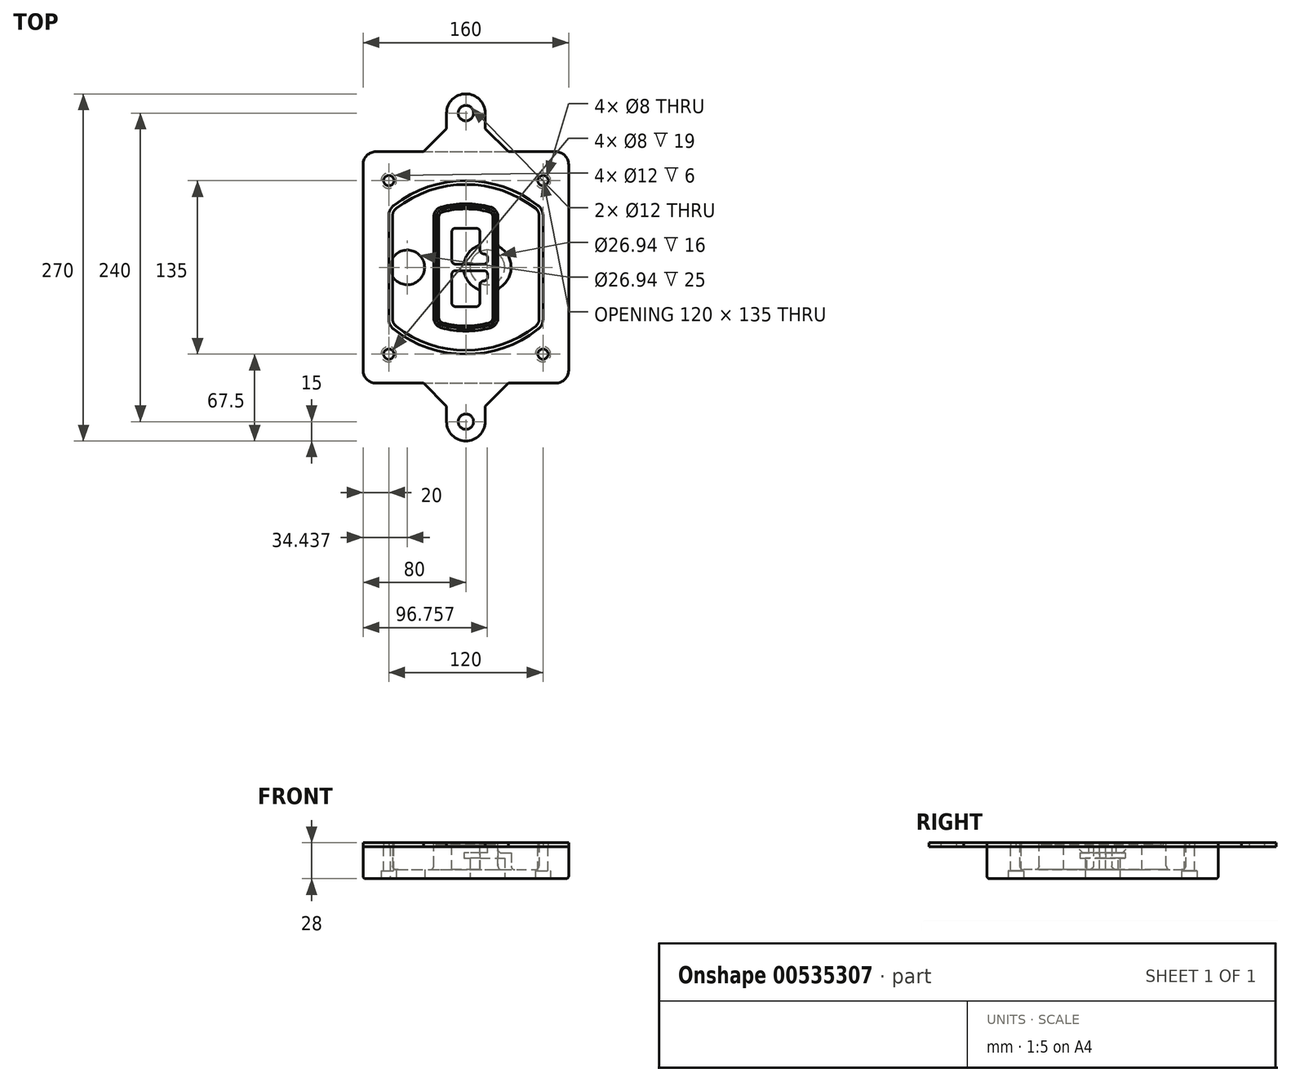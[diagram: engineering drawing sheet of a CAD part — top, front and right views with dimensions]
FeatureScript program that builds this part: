
annotation { "Feature Type Name" : "Feature", "Feature Type Description" : "" }
export const myFeature = defineFeature(function(context is Context, id is Id, definition is map)
    precondition{}
    {
        {
            var Q0;
            Q0=qCreatedBy(makeId("Top.planeOp"),FACE);
            var sketch = newSketch(context, id + "F0", { "sketchPlane" : qUnion([Q0])});
            skPoint(sketch, "E0.rect.middle", {"position": v(0, 0) * mm});
            skLineSegment(sketch, "E1.bottom", {"start": v(-70, -90) * mm, "end": v(70, -90) * mm});
            skLineSegment(sketch, "E1.top", {"start": v(-70, 90) * mm, "end": v(70, 90) * mm});
            skLineSegment(sketch, "E1.left", {"start": v(-80, -80) * mm, "end": v(-80, 80) * mm});
            skLineSegment(sketch, "E1.right", {"start": v(80, -80) * mm, "end": v(80, 80) * mm});
            skLineSegment(sketch, "E2", {"start": v(-80, 90) * mm, "end": v(80, -90) * mm, "construction": true});
            skLineSegment(sketch, "E3", {"start": v(80, 90) * mm, "end": v(-80, -90) * mm, "construction": true});
            skCircle(sketch, "E4", {"center": v(-60, 67.5) * mm, "radius": 4 * mm});
            skCircle(sketch, "E5", {"center": v(60, 67.5) * mm, "radius": 4 * mm});
            skCircle(sketch, "E6", {"center": v(60, -67.5) * mm, "radius": 4 * mm});
            skCircle(sketch, "E7", {"center": v(-60, -67.5) * mm, "radius": 4 * mm});
            skLineSegment(sketch, "E8", {"start": v(-60, 67.5) * mm, "end": v(60, 67.5) * mm, "construction": true});
            skLineSegment(sketch, "E9", {"start": v(60, 67.5) * mm, "end": v(60, -67.5) * mm, "construction": true});
            skLineSegment(sketch, "E10", {"start": v(60, -67.5) * mm, "end": v(-60, -67.5) * mm, "construction": true});
            skLineSegment(sketch, "E11", {"start": v(-60, -67.5) * mm, "end": v(-60, 67.5) * mm, "construction": true});
            skLineSegment(sketch, "E12", {"start": v(-60, 40.3) * mm, "end": v(-60, -40.3) * mm});
            skLineSegment(sketch, "E13", {"start": v(60, 40.3) * mm, "end": v(60, -40.3) * mm});
            skArc(sketch, "E14", {"start": v(56.15, 48.18) * mm, "mid": v(0, 67.5) * mm, "end": v(-56.15, 48.18) * mm});
            skArc(sketch, "E15", {"start": v(-56.15, -48.18) * mm, "mid": v(0, -67.5) * mm, "end": v(56.15, -48.18) * mm});
            skLineSegment(sketch, "E16", {"start": v(-60, 0) * mm, "end": v(60, 0) * mm, "construction": true});
            skPoint(sketch, "E17.visualSharp", {"position": v(-60, -45) * mm});
            skArc(sketch, "E17.filletArc", {"start": v(-60, -40.3) * mm, "mid": v(-58.99, -44.68) * mm, "end": v(-56.15, -48.18) * mm});
            skPoint(sketch, "E18.visualSharp", {"position": v(-60, 45) * mm});
            skArc(sketch, "E18.filletArc", {"start": v(-56.15, 48.18) * mm, "mid": v(-58.99, 44.68) * mm, "end": v(-60, 40.3) * mm});
            skPoint(sketch, "E19.visualSharp", {"position": v(60, 45) * mm});
            skArc(sketch, "E19.filletArc", {"start": v(60, 40.3) * mm, "mid": v(58.99, 44.68) * mm, "end": v(56.15, 48.18) * mm});
            skPoint(sketch, "E20.visualSharp", {"position": v(60, -45) * mm});
            skArc(sketch, "E20.filletArc", {"start": v(56.15, -48.18) * mm, "mid": v(58.99, -44.68) * mm, "end": v(60, -40.3) * mm});
            skPoint(sketch, "E21.visualSharp", {"position": v(-80, 90) * mm});
            skArc(sketch, "E21.filletArc", {"start": v(-70, 90) * mm, "mid": v(-77.07, 87.07) * mm, "end": v(-80, 80) * mm});
            skPoint(sketch, "E22.visualSharp", {"position": v(80, 90) * mm});
            skArc(sketch, "E22.filletArc", {"start": v(80, 80) * mm, "mid": v(77.07, 87.07) * mm, "end": v(70, 90) * mm});
            skPoint(sketch, "E23.visualSharp", {"position": v(80, -90) * mm});
            skArc(sketch, "E23.filletArc", {"start": v(70, -90) * mm, "mid": v(77.07, -87.07) * mm, "end": v(80, -80) * mm});
            skPoint(sketch, "E24.visualSharp", {"position": v(-80, -90) * mm});
            skArc(sketch, "E24.filletArc", {"start": v(-80, -80) * mm, "mid": v(-77.07, -87.07) * mm, "end": v(-70, -90) * mm});
            skArc(sketch, "E25.0", {"start": v(57, 40.3) * mm, "mid": v(56.3, 43.36) * mm, "end": v(54.3, 45.81) * mm});
            skLineSegment(sketch, "E25.1", {"start": v(57, 40.3) * mm, "end": v(57, -40.3) * mm});
            skArc(sketch, "E25.2", {"start": v(54.3, -45.81) * mm, "mid": v(56.3, -43.36) * mm, "end": v(57, -40.3) * mm});
            skArc(sketch, "E25.3", {"start": v(-54.3, -45.81) * mm, "mid": v(0, -64.5) * mm, "end": v(54.3, -45.81) * mm});
            skArc(sketch, "E25.4", {"start": v(-57, -40.3) * mm, "mid": v(-56.3, -43.36) * mm, "end": v(-54.3, -45.81) * mm});
            skArc(sketch, "E25.5", {"start": v(54.3, 45.81) * mm, "mid": v(0, 64.5) * mm, "end": v(-54.3, 45.81) * mm});
            skLineSegment(sketch, "E25.6", {"start": v(-57, 40.3) * mm, "end": v(-57, -40.3) * mm});
            skArc(sketch, "E25.7", {"start": v(-54.3, 45.81) * mm, "mid": v(-56.3, 43.36) * mm, "end": v(-57, 40.3) * mm});
            skArc(sketch, "E26.0", {"start": v(-58.62, 51.33) * mm, "mid": v(-62.58, 46.43) * mm, "end": v(-64, 40.3) * mm});
            skArc(sketch, "E26.1", {"start": v(58.62, 51.33) * mm, "mid": v(0, 71.5) * mm, "end": v(-58.62, 51.33) * mm});
            skArc(sketch, "E26.2", {"start": v(64, 40.3) * mm, "mid": v(62.58, 46.43) * mm, "end": v(58.62, 51.33) * mm});
            skLineSegment(sketch, "E26.3", {"start": v(64, 40.3) * mm, "end": v(64, -40.3) * mm});
            skArc(sketch, "E26.4", {"start": v(58.62, -51.33) * mm, "mid": v(62.58, -46.43) * mm, "end": v(64, -40.3) * mm});
            skLineSegment(sketch, "E26.5", {"start": v(-64, 40.3) * mm, "end": v(-64, -40.3) * mm});
            skArc(sketch, "E26.6", {"start": v(-58.62, -51.33) * mm, "mid": v(0, -71.5) * mm, "end": v(58.62, -51.33) * mm});
            skArc(sketch, "E26.7", {"start": v(-64, -40.3) * mm, "mid": v(-62.58, -46.43) * mm, "end": v(-58.62, -51.33) * mm});
            skSolve(sketch);
        }
        {
            var Q0;
            Q0=makeQuery(id+"F0.imprint","IMPRINT",FACE,{"disambiguationData":[TD([[makeQuery(id+"F0.imprint","IMPRINT",EDGE,{"derivedFrom":sQuery(id+"F0.wireOp",EDGE,"E1.bottom")}),1.0]])]});
            var Q1;
            Q1=makeQuery(id+"F0.imprint","IMPRINT",FACE,{"disambiguationData":[TD([[makeQuery(id+"F0.imprint","IMPRINT",EDGE,{"derivedFrom":sQuery(id+"F0.wireOp",EDGE,"E12")}),1.0]])]});
            var Q2;
            Q2=makeQuery(id+"F0.imprint","IMPRINT",FACE,{"disambiguationData":[TD([[makeQuery(id+"F0.imprint","IMPRINT",EDGE,{"derivedFrom":sQuery(id+"F0.wireOp",EDGE,"E25.0")}),1.0]])]});
            var Q3;
            Q3=makeQuery(id+"F0.imprint","IMPRINT",FACE,{"disambiguationData":[TD([[makeQuery(id+"F0.imprint","IMPRINT",EDGE,{"derivedFrom":sQuery(id+"F0.wireOp",EDGE,"E12")}),-1.0]])]});
            extrude(context, id + "F1", {"entities" : qUnion([Q0, Q1, Q2, Q3]), "oppositeDirection" : true, "depth" : 25 * mm});
        }
        {
            var Q0;
            Q0=makeQuery(id+"F0.imprint","IMPRINT",FACE,{"disambiguationData":[TD([[makeQuery(id+"F0.imprint","IMPRINT",EDGE,{"derivedFrom":sQuery(id+"F0.wireOp",EDGE,"E12")}),1.0]])]});
            extrude(context, id + "F2", {"entities" : qUnion([Q0]), "operationType" : NewBodyOperationType.ADD, "depth" : 3 * mm});
        }
        {
            var Q0;
            Q0=makeQuery(id+"F0.imprint","IMPRINT",FACE,{"disambiguationData":[TD([[makeQuery(id+"F0.imprint","IMPRINT",EDGE,{"derivedFrom":sQuery(id+"F0.wireOp",EDGE,"E25.0")}),1.0]])]});
            extrude(context, id + "F3", {"entities" : qUnion([Q0]), "operationType" : NewBodyOperationType.REMOVE, "oppositeDirection" : true, "depth" : 18 * mm});
        }
        {
            var Q0;
            Q0=makeQuery(id+"F2.opExtrude","CAP_FACE",FACE,{"disambiguationData":[OSD([sQuery(id+"F0.wireOp",EDGE,"E12"),sQuery(id+"F0.wireOp",EDGE,"E13"),sQuery(id+"F0.wireOp",EDGE,"E14"),sQuery(id+"F0.wireOp",EDGE,"E15"),sQuery(id+"F0.wireOp",EDGE,"E17.filletArc"),sQuery(id+"F0.wireOp",EDGE,"E18.filletArc"),sQuery(id+"F0.wireOp",EDGE,"E19.filletArc"),sQuery(id+"F0.wireOp",EDGE,"E20.filletArc"),sQuery(id+"F0.wireOp",EDGE,"E25.0"),sQuery(id+"F0.wireOp",EDGE,"E25.1"),sQuery(id+"F0.wireOp",EDGE,"E25.2"),sQuery(id+"F0.wireOp",EDGE,"E25.3"),sQuery(id+"F0.wireOp",EDGE,"E25.4"),sQuery(id+"F0.wireOp",EDGE,"E25.5"),sQuery(id+"F0.wireOp",EDGE,"E25.6"),sQuery(id+"F0.wireOp",EDGE,"E25.7")])],"isStart":false});
            var sketch = newSketch(context, id + "F4", { "sketchPlane" : qUnion([Q0])});
            skArc(sketch, "E27.0", {"start": v(-19.08, -46.97) * mm, "mid": v(0, -49.5) * mm, "end": v(19.08, -46.97) * mm});
            skArc(sketch, "E28.0", {"start": v(19.08, 46.97) * mm, "mid": v(0, 49.5) * mm, "end": v(-19.08, 46.97) * mm});
            skLineSegment(sketch, "E29", {"start": v(-25, 39.25) * mm, "end": v(-25, -39.25) * mm});
            skLineSegment(sketch, "E30", {"start": v(25, 39.25) * mm, "end": v(25, -39.25) * mm});
            skLineSegment(sketch, "E31", {"start": v(-25, 45.1) * mm, "end": v(25, 45.1) * mm, "construction": true});
            skLineSegment(sketch, "E32", {"start": v(-25, -45.1) * mm, "end": v(25, -45.1) * mm, "construction": true});
            skPoint(sketch, "E33.visualSharp", {"position": v(-25, 45.1) * mm});
            skArc(sketch, "E33.filletArc", {"start": v(-19.08, 46.97) * mm, "mid": v(-23.35, 44.11) * mm, "end": v(-25, 39.25) * mm});
            skPoint(sketch, "E34.visualSharp", {"position": v(25, 45.1) * mm});
            skArc(sketch, "E34.filletArc", {"start": v(25, 39.25) * mm, "mid": v(23.35, 44.11) * mm, "end": v(19.08, 46.97) * mm});
            skPoint(sketch, "E35.visualSharp", {"position": v(25, -45.1) * mm});
            skArc(sketch, "E35.filletArc", {"start": v(19.08, -46.97) * mm, "mid": v(23.35, -44.11) * mm, "end": v(25, -39.25) * mm});
            skPoint(sketch, "E36.visualSharp", {"position": v(-25, -45.1) * mm});
            skArc(sketch, "E36.filletArc", {"start": v(-25, -39.25) * mm, "mid": v(-23.35, -44.11) * mm, "end": v(-19.08, -46.97) * mm});
            skArc(sketch, "E37.0", {"start": v(54.3, 45.81) * mm, "mid": v(0, 64.5) * mm, "end": v(-54.3, 45.81) * mm});
            skArc(sketch, "E37.1", {"start": v(-54.3, 45.81) * mm, "mid": v(-56.3, 43.36) * mm, "end": v(-57, 40.3) * mm});
            skLineSegment(sketch, "E37.2", {"start": v(-57, 40.3) * mm, "end": v(-57, -40.3) * mm});
            skArc(sketch, "E37.3", {"start": v(-57, -40.3) * mm, "mid": v(-56.3, -43.36) * mm, "end": v(-54.3, -45.81) * mm});
            skArc(sketch, "E37.4", {"start": v(-54.3, -45.81) * mm, "mid": v(0, -64.5) * mm, "end": v(54.3, -45.81) * mm});
            skArc(sketch, "E37.5", {"start": v(54.3, -45.81) * mm, "mid": v(56.3, -43.36) * mm, "end": v(57, -40.3) * mm});
            skLineSegment(sketch, "E37.6", {"start": v(57, 40.3) * mm, "end": v(57, -40.3) * mm});
            skArc(sketch, "E37.7", {"start": v(57, 40.3) * mm, "mid": v(56.3, 43.36) * mm, "end": v(54.3, 45.81) * mm});
            skLineSegment(sketch, "E38.0", {"start": v(23, 39.25) * mm, "end": v(23, -39.25) * mm});
            skArc(sketch, "E38.1", {"start": v(18.56, -45.04) * mm, "mid": v(21.76, -42.9) * mm, "end": v(23, -39.25) * mm});
            skArc(sketch, "E38.2", {"start": v(-18.56, -45.04) * mm, "mid": v(0, -47.5) * mm, "end": v(18.56, -45.04) * mm});
            skArc(sketch, "E38.3", {"start": v(-23, -39.25) * mm, "mid": v(-21.76, -42.9) * mm, "end": v(-18.56, -45.04) * mm});
            skLineSegment(sketch, "E38.4", {"start": v(-23, 39.25) * mm, "end": v(-23, -39.25) * mm});
            skArc(sketch, "E38.5", {"start": v(23, 39.25) * mm, "mid": v(21.76, 42.9) * mm, "end": v(18.56, 45.04) * mm});
            skArc(sketch, "E38.6", {"start": v(-18.56, 45.04) * mm, "mid": v(-21.76, 42.9) * mm, "end": v(-23, 39.25) * mm});
            skArc(sketch, "E38.7", {"start": v(18.56, 45.04) * mm, "mid": v(0, 47.5) * mm, "end": v(-18.56, 45.04) * mm});
            skArc(sketch, "E39.0", {"start": v(21, 39.25) * mm, "mid": v(20.18, 41.68) * mm, "end": v(18.04, 43.1) * mm});
            skLineSegment(sketch, "E39.1", {"start": v(21, 39.25) * mm, "end": v(21, -39.25) * mm});
            skArc(sketch, "E39.2", {"start": v(18.04, -43.1) * mm, "mid": v(20.18, -41.68) * mm, "end": v(21, -39.25) * mm});
            skArc(sketch, "E39.3", {"start": v(-18.04, -43.1) * mm, "mid": v(0, -45.5) * mm, "end": v(18.04, -43.1) * mm});
            skArc(sketch, "E39.4", {"start": v(-21, -39.25) * mm, "mid": v(-20.18, -41.68) * mm, "end": v(-18.04, -43.1) * mm});
            skArc(sketch, "E39.5", {"start": v(18.04, 43.1) * mm, "mid": v(0, 45.5) * mm, "end": v(-18.04, 43.1) * mm});
            skLineSegment(sketch, "E39.6", {"start": v(-21, 39.25) * mm, "end": v(-21, -39.25) * mm});
            skArc(sketch, "E39.7", {"start": v(-18.04, 43.1) * mm, "mid": v(-20.18, 41.68) * mm, "end": v(-21, 39.25) * mm});
            skLineSegment(sketch, "E40", {"start": v(-25, 0) * mm, "end": v(25, 0) * mm, "construction": true});
            skLineSegment(sketch, "E41", {"start": v(-11, 5.5) * mm, "end": v(-11, 27.5) * mm});
            skLineSegment(sketch, "E42", {"start": v(-8, 30.5) * mm, "end": v(8, 30.5) * mm});
            skLineSegment(sketch, "E43", {"start": v(11, 27.5) * mm, "end": v(11, 13.5) * mm});
            skLineSegment(sketch, "E44", {"start": v(14, 10.5) * mm, "end": v(14, 10.5) * mm});
            skLineSegment(sketch, "E45", {"start": v(17, 7.5) * mm, "end": v(17, 5.5) * mm});
            skLineSegment(sketch, "E46", {"start": v(14, 2.5) * mm, "end": v(-8, 2.5) * mm});
            skPoint(sketch, "E47.visualSharp", {"position": v(-11, 30.5) * mm});
            skArc(sketch, "E47.filletArc", {"start": v(-8, 30.5) * mm, "mid": v(-10.12, 29.62) * mm, "end": v(-11, 27.5) * mm});
            skPoint(sketch, "E48.visualSharp", {"position": v(11, 30.5) * mm});
            skArc(sketch, "E48.filletArc", {"start": v(11, 27.5) * mm, "mid": v(10.12, 29.62) * mm, "end": v(8, 30.5) * mm});
            skPoint(sketch, "E49.visualSharp", {"position": v(11, 10.5) * mm});
            skArc(sketch, "E49.filletArc", {"start": v(11, 13.5) * mm, "mid": v(11.88, 11.38) * mm, "end": v(14, 10.5) * mm});
            skPoint(sketch, "E50.visualSharp", {"position": v(17, 10.5) * mm});
            skArc(sketch, "E50.filletArc", {"start": v(17, 7.5) * mm, "mid": v(16.12, 9.62) * mm, "end": v(14, 10.5) * mm});
            skPoint(sketch, "E51.visualSharp", {"position": v(17, 2.5) * mm});
            skArc(sketch, "E51.filletArc", {"start": v(14, 2.5) * mm, "mid": v(16.12, 3.38) * mm, "end": v(17, 5.5) * mm});
            skPoint(sketch, "E52.visualSharp", {"position": v(-11, 2.5) * mm});
            skArc(sketch, "E52.filletArc", {"start": v(-11, 5.5) * mm, "mid": v(-10.12, 3.38) * mm, "end": v(-8, 2.5) * mm});
            skLineSegment(sketch, "E53.0.MirrorCS", {"start": v(14, -2.5) * mm, "end": v(-8, -2.5) * mm});
            skArc(sketch, "E54.0.MirrorCS", {"start": v(-11, -5.5) * mm, "mid": v(-10.12, -3.38) * mm, "end": v(-8, -2.5) * mm});
            skLineSegment(sketch, "E55.0.MirrorCS", {"start": v(-11, -5.5) * mm, "end": v(-11, -27.5) * mm});
            skArc(sketch, "E56.0.MirrorCS", {"start": v(-8, -30.5) * mm, "mid": v(-10.12, -29.62) * mm, "end": v(-11, -27.5) * mm});
            skLineSegment(sketch, "E57.0.MirrorCS", {"start": v(-8, -30.5) * mm, "end": v(8, -30.5) * mm});
            skArc(sketch, "E58.0.MirrorCS", {"start": v(11, -27.5) * mm, "mid": v(10.12, -29.62) * mm, "end": v(8, -30.5) * mm});
            skLineSegment(sketch, "E59.0.MirrorCS", {"start": v(11, -27.5) * mm, "end": v(11, -13.5) * mm});
            skArc(sketch, "E60.0.MirrorCS", {"start": v(11, -13.5) * mm, "mid": v(11.88, -11.38) * mm, "end": v(14, -10.5) * mm});
            skArc(sketch, "E61.0.MirrorCS", {"start": v(17, -7.5) * mm, "mid": v(16.12, -9.62) * mm, "end": v(14, -10.5) * mm});
            skLineSegment(sketch, "E62.0.MirrorCS", {"start": v(17, -7.5) * mm, "end": v(17, -5.5) * mm});
            skArc(sketch, "E63.0.MirrorCS", {"start": v(14, -2.5) * mm, "mid": v(16.12, -3.38) * mm, "end": v(17, -5.5) * mm});
            skSolve(sketch);
        }
        {
            var Q0;
            Q0=makeQuery(id+"F4.imprint","IMPRINT",FACE,{"disambiguationData":[TD([[makeQuery(id+"F4.imprint","IMPRINT",EDGE,{"derivedFrom":sQuery(id+"F4.wireOp",EDGE,"E27.0")}),1.0]])]});
            var Q1;
            Q1=makeQuery(id+"F4.imprint","IMPRINT",FACE,{"disambiguationData":[TD([[makeQuery(id+"F4.imprint","IMPRINT",EDGE,{"derivedFrom":sQuery(id+"F4.wireOp",EDGE,"E38.0")}),-1.0]])]});
            var Q2;
            Q2=makeQuery(id+"F4.imprint","IMPRINT",FACE,{"disambiguationData":[TD([[makeQuery(id+"F4.imprint","IMPRINT",EDGE,{"derivedFrom":sQuery(id+"F4.wireOp",EDGE,"E39.0")}),1.0]])]});
            extrude(context, id + "F5", {"entities" : qUnion([Q0, Q1, Q2]), "operationType" : NewBodyOperationType.ADD, "endBound" : BoundingType.UP_TO_NEXT, "oppositeDirection" : true, "depth" : 25 * mm});
        }
        {
            var Q0;
            Q0=makeQuery(id+"F4.imprint","IMPRINT",FACE,{"disambiguationData":[TD([[makeQuery(id+"F4.imprint","IMPRINT",EDGE,{"derivedFrom":sQuery(id+"F4.wireOp",EDGE,"E38.0")}),-1.0]])]});
            extrude(context, id + "F6", {"entities" : qUnion([Q0]), "operationType" : NewBodyOperationType.REMOVE, "oppositeDirection" : true, "depth" : 2 * mm});
        }
        {
            var Q0;
            Q0=makeQuery(id+"F1.opExtrude","CAP_FACE",FACE,{"disambiguationData":[OSD([sQuery(id+"F0.wireOp",EDGE,"E1.bottom"),sQuery(id+"F0.wireOp",EDGE,"E1.top"),sQuery(id+"F0.wireOp",EDGE,"E1.left"),sQuery(id+"F0.wireOp",EDGE,"E1.right"),sQuery(id+"F0.wireOp",EDGE,"E4"),sQuery(id+"F0.wireOp",EDGE,"E5"),sQuery(id+"F0.wireOp",EDGE,"E6"),sQuery(id+"F0.wireOp",EDGE,"E7"),sQuery(id+"F0.wireOp",EDGE,"E21.filletArc"),sQuery(id+"F0.wireOp",EDGE,"E22.filletArc"),sQuery(id+"F0.wireOp",EDGE,"E23.filletArc"),sQuery(id+"F0.wireOp",EDGE,"E24.filletArc")])],"isStart":false});
            var sketch = newSketch(context, id + "F7", { "sketchPlane" : qUnion([Q0])});
            skCircle(sketch, "E64", {"center": v(16.76, 0) * mm, "radius": 13.47 * mm});
            skCircle(sketch, "E65", {"center": v(-45.56, 0) * mm, "radius": 13.47 * mm});
            skLineSegment(sketch, "E66", {"start": v(80, 0) * mm, "end": v(-80, 0) * mm});
            skCircle(sketch, "E67", {"center": v(16.76, 0) * mm, "radius": 18.47 * mm});
            skCircle(sketch, "E68", {"center": v(60, -67.5) * mm, "radius": 6 * mm});
            skCircle(sketch, "E69", {"center": v(-60, -67.5) * mm, "radius": 6 * mm});
            skCircle(sketch, "E70", {"center": v(-60, 67.5) * mm, "radius": 6 * mm});
            skCircle(sketch, "E71", {"center": v(60, 67.5) * mm, "radius": 6 * mm});
            skSolve(sketch);
        }
        {
            var Q0;
            {var subQ1=sQuery(id+"F7.wireOp",EDGE,"E66");var subQ4=sQuery(id+"F7.wireOp",EDGE,"E64");var subQ6=makeQuery(id+"F7.imprint","INTERSECT",VERTEX,{"disambiguationData":[OD(0.0)],"derivedFrom":[subQ4,subQ1]});Q0=makeQuery(id+"F7.imprint","IMPRINT",FACE,{"disambiguationData":[TD([[makeQuery(id+"F7.imprint","IMPRINT",EDGE,{"disambiguationData":[TD([[subQ6,-1.0]])],"derivedFrom":subQ4}),-1.0]])]});}
            var Q1;
            {var subQ0=sQuery(id+"F7.wireOp",EDGE,"E66");var subQ1=sQuery(id+"F7.wireOp",EDGE,"E64");var subQ3=makeQuery(id+"F7.imprint","INTERSECT",VERTEX,{"disambiguationData":[OD(0.0)],"derivedFrom":[subQ1,subQ0]});Q1=makeQuery(id+"F7.imprint","IMPRINT",FACE,{"disambiguationData":[TD([[makeQuery(id+"F7.imprint","IMPRINT",EDGE,{"disambiguationData":[TD([[subQ3,-1.0]])],"derivedFrom":subQ1}),1.0]])]});}
            var Q2;
            {var subQ0=sQuery(id+"F7.wireOp",EDGE,"E66");var subQ1=sQuery(id+"F7.wireOp",EDGE,"E64");var subQ3=makeQuery(id+"F7.imprint","INTERSECT",VERTEX,{"disambiguationData":[OD(0.0)],"derivedFrom":[subQ1,subQ0]});Q2=makeQuery(id+"F7.imprint","IMPRINT",FACE,{"disambiguationData":[TD([[makeQuery(id+"F7.imprint","IMPRINT",EDGE,{"disambiguationData":[TD([[subQ3,1.0]])],"derivedFrom":subQ1}),1.0]])]});}
            var Q3;
            {var subQ1=sQuery(id+"F7.wireOp",EDGE,"E66");var subQ4=sQuery(id+"F7.wireOp",EDGE,"E64");var subQ6=makeQuery(id+"F7.imprint","INTERSECT",VERTEX,{"disambiguationData":[OD(0.0)],"derivedFrom":[subQ4,subQ1]});Q3=makeQuery(id+"F7.imprint","IMPRINT",FACE,{"disambiguationData":[TD([[makeQuery(id+"F7.imprint","IMPRINT",EDGE,{"disambiguationData":[TD([[subQ6,1.0]])],"derivedFrom":subQ4}),-1.0]])]});}
            extrude(context, id + "F8", {"entities" : qUnion([Q0, Q1, Q2, Q3]), "operationType" : NewBodyOperationType.ADD, "oppositeDirection" : true, "depth" : 20 * mm});
        }
        {
            var Q0;
            {var subQ0=sQuery(id+"F7.wireOp",EDGE,"E66");var subQ1=sQuery(id+"F7.wireOp",EDGE,"E64");var subQ3=makeQuery(id+"F7.imprint","INTERSECT",VERTEX,{"disambiguationData":[OD(0.0)],"derivedFrom":[subQ1,subQ0]});Q0=makeQuery(id+"F7.imprint","IMPRINT",FACE,{"disambiguationData":[TD([[makeQuery(id+"F7.imprint","IMPRINT",EDGE,{"disambiguationData":[TD([[subQ3,-1.0]])],"derivedFrom":subQ1}),1.0]])]});}
            var Q1;
            {var subQ0=sQuery(id+"F7.wireOp",EDGE,"E66");var subQ1=sQuery(id+"F7.wireOp",EDGE,"E64");var subQ3=makeQuery(id+"F7.imprint","INTERSECT",VERTEX,{"disambiguationData":[OD(0.0)],"derivedFrom":[subQ1,subQ0]});Q1=makeQuery(id+"F7.imprint","IMPRINT",FACE,{"disambiguationData":[TD([[makeQuery(id+"F7.imprint","IMPRINT",EDGE,{"disambiguationData":[TD([[subQ3,1.0]])],"derivedFrom":subQ1}),1.0]])]});}
            extrude(context, id + "F9", {"entities" : qUnion([Q0, Q1]), "operationType" : NewBodyOperationType.REMOVE, "oppositeDirection" : true, "depth" : 16 * mm});
        }
        {
            var Q0;
            {var subQ0=sQuery(id+"F7.wireOp",EDGE,"E66");var subQ1=sQuery(id+"F7.wireOp",EDGE,"E65");var subQ3=makeQuery(id+"F7.imprint","INTERSECT",VERTEX,{"disambiguationData":[OD(0.0)],"derivedFrom":[subQ1,subQ0]});Q0=makeQuery(id+"F7.imprint","IMPRINT",FACE,{"disambiguationData":[TD([[makeQuery(id+"F7.imprint","IMPRINT",EDGE,{"disambiguationData":[TD([[subQ3,-1.0]])],"derivedFrom":subQ1}),1.0]])]});}
            var Q1;
            {var subQ0=sQuery(id+"F7.wireOp",EDGE,"E66");var subQ1=sQuery(id+"F7.wireOp",EDGE,"E65");var subQ3=makeQuery(id+"F7.imprint","INTERSECT",VERTEX,{"disambiguationData":[OD(0.0)],"derivedFrom":[subQ1,subQ0]});Q1=makeQuery(id+"F7.imprint","IMPRINT",FACE,{"disambiguationData":[TD([[makeQuery(id+"F7.imprint","IMPRINT",EDGE,{"disambiguationData":[TD([[subQ3,1.0]])],"derivedFrom":subQ1}),1.0]])]});}
            extrude(context, id + "F10", {"entities" : qUnion([Q0, Q1]), "operationType" : NewBodyOperationType.REMOVE, "oppositeDirection" : true, "depth" : 25 * mm});
        }
        {
            var Q0;
            Q0=makeQuery(id+"F7.imprint","IMPRINT",FACE,{"disambiguationData":[TD([[makeQuery(id+"F7.imprint","IMPRINT",EDGE,{"derivedFrom":sQuery(id+"F7.wireOp",EDGE,"E68")}),1.0]])]});
            var Q1;
            Q1=makeQuery(id+"F7.imprint","IMPRINT",FACE,{"disambiguationData":[TD([[makeQuery(id+"F7.imprint","IMPRINT",EDGE,{"derivedFrom":makeQuery(id+"F1.opExtrude","CAP_EDGE",EDGE,{"disambiguationData":[OSD([sQuery(id+"F0.wireOp",EDGE,"E5")])],"isStart":false})}),-1.0]])]});
            var Q2;
            Q2=makeQuery(id+"F7.imprint","IMPRINT",FACE,{"disambiguationData":[TD([[makeQuery(id+"F7.imprint","IMPRINT",EDGE,{"derivedFrom":sQuery(id+"F7.wireOp",EDGE,"E69")}),1.0]])]});
            var Q3;
            Q3=makeQuery(id+"F7.imprint","IMPRINT",FACE,{"disambiguationData":[TD([[makeQuery(id+"F7.imprint","IMPRINT",EDGE,{"derivedFrom":makeQuery(id+"F1.opExtrude","CAP_EDGE",EDGE,{"disambiguationData":[OSD([sQuery(id+"F0.wireOp",EDGE,"E4")])],"isStart":false})}),-1.0]])]});
            var Q4;
            Q4=makeQuery(id+"F7.imprint","IMPRINT",FACE,{"disambiguationData":[TD([[makeQuery(id+"F7.imprint","IMPRINT",EDGE,{"derivedFrom":sQuery(id+"F7.wireOp",EDGE,"E70")}),1.0]])]});
            var Q5;
            Q5=makeQuery(id+"F7.imprint","IMPRINT",FACE,{"disambiguationData":[TD([[makeQuery(id+"F7.imprint","IMPRINT",EDGE,{"derivedFrom":makeQuery(id+"F1.opExtrude","CAP_EDGE",EDGE,{"disambiguationData":[OSD([sQuery(id+"F0.wireOp",EDGE,"E7")])],"isStart":false})}),-1.0]])]});
            var Q6;
            Q6=makeQuery(id+"F7.imprint","IMPRINT",FACE,{"disambiguationData":[TD([[makeQuery(id+"F7.imprint","IMPRINT",EDGE,{"derivedFrom":sQuery(id+"F7.wireOp",EDGE,"E71")}),1.0]])]});
            var Q7;
            Q7=makeQuery(id+"F7.imprint","IMPRINT",FACE,{"disambiguationData":[TD([[makeQuery(id+"F7.imprint","IMPRINT",EDGE,{"derivedFrom":makeQuery(id+"F1.opExtrude","CAP_EDGE",EDGE,{"disambiguationData":[OSD([sQuery(id+"F0.wireOp",EDGE,"E6")])],"isStart":false})}),-1.0]])]});
            extrude(context, id + "F11", {"entities" : qUnion([Q0, Q1, Q2, Q3, Q4, Q5, Q6, Q7]), "operationType" : NewBodyOperationType.REMOVE, "oppositeDirection" : true, "depth" : 6 * mm});
        }
        {
            var Q0;
            Q0=makeQuery(id+"F9.boolean.opBoolean","COPY",FACE,{"derivedFrom":makeQuery(id+"F9.opExtrude","CAP_FACE",FACE,{"disambiguationData":[OSD([sQuery(id+"F7.wireOp",EDGE,"E64")])],"isStart":false})});
            var sketch = newSketch(context, id + "F12", { "sketchPlane" : qUnion([Q0])});
            skArc(sketch, "E72.0", {"start": v(11, 17.55) * mm, "mid": v(2.57, 11.82) * mm, "end": v(-1.54, 2.5) * mm});
            skArc(sketch, "E72.1", {"start": v(-1.54, -2.5) * mm, "mid": v(2.57, -11.82) * mm, "end": v(11, -17.55) * mm});
            skLineSegment(sketch, "E73", {"start": v(-1.54, -2.5) * mm, "end": v(14, -2.5) * mm});
            skLineSegment(sketch, "E74.0", {"start": v(14, 2.5) * mm, "end": v(-1.54, 2.5) * mm});
            skArc(sketch, "E74.1", {"start": v(14, 2.5) * mm, "mid": v(16.12, 3.38) * mm, "end": v(17, 5.5) * mm});
            skLineSegment(sketch, "E74.2", {"start": v(17, 7.5) * mm, "end": v(17, 5.5) * mm});
            skArc(sketch, "E74.3", {"start": v(17, 7.5) * mm, "mid": v(16.12, 9.62) * mm, "end": v(14, 10.5) * mm});
            skArc(sketch, "E74.4", {"start": v(11, 13.5) * mm, "mid": v(11.88, 11.38) * mm, "end": v(14, 10.5) * mm});
            skLineSegment(sketch, "E74.5", {"start": v(11, 17.55) * mm, "end": v(11, 13.5) * mm});
            skLineSegment(sketch, "E74.7", {"start": v(14, -2.5) * mm, "end": v(-1.54, -2.5) * mm});
            skArc(sketch, "E74.8", {"start": v(14, -2.5) * mm, "mid": v(16.12, -3.38) * mm, "end": v(17, -5.5) * mm});
            skLineSegment(sketch, "E74.9", {"start": v(17, -7.5) * mm, "end": v(17, -5.5) * mm});
            skArc(sketch, "E74.10", {"start": v(17, -7.5) * mm, "mid": v(16.12, -9.62) * mm, "end": v(14, -10.5) * mm});
            skArc(sketch, "E74.11", {"start": v(11, -13.5) * mm, "mid": v(11.88, -11.38) * mm, "end": v(14, -10.5) * mm});
            skLineSegment(sketch, "E74.12", {"start": v(11, -17.55) * mm, "end": v(11, -13.5) * mm});
            skPoint(sketch, "E75.orphan", {"position": v(11, -27.5) * mm});
            skPoint(sketch, "E76.orphan", {"position": v(-8, -2.5) * mm});
            skPoint(sketch, "E77.orphan", {"position": v(-8, 2.5) * mm});
            skPoint(sketch, "E78.orphan", {"position": v(11, 27.5) * mm});
            skSolve(sketch);
        }
        {
            var Q0;
            {var subQ7=sQuery(id+"F12.wireOp",EDGE,"E72.0");var subQ14=sQuery(id+"F12.wireOp",EDGE,"E72.1");var subQ16=sQuery(id+"F12.wireOp",EDGE,"E74.1");var subQ18=sQuery(id+"F12.wireOp",EDGE,"E74.8");Q0=qUnion([makeQuery(id+"F12.imprint","IMPRINT",FACE,{"disambiguationData":[TD([[makeQuery(id+"F12.imprint","IMPRINT",EDGE,{"derivedFrom":subQ7}),1.0]])]}),makeQuery(id+"F12.imprint","IMPRINT",FACE,{"disambiguationData":[TD([[makeQuery(id+"F12.imprint","IMPRINT",EDGE,{"derivedFrom":subQ14}),1.0]])]}),makeQuery(id+"F12.imprint","IMPRINT",FACE,{"disambiguationData":[TD([[makeQuery(id+"F12.imprint","IMPRINT",EDGE,{"derivedFrom":subQ16}),1.0]])]}),makeQuery(id+"F12.imprint","IMPRINT",FACE,{"disambiguationData":[TD([[makeQuery(id+"F12.imprint","IMPRINT",EDGE,{"derivedFrom":subQ18}),-1.0]])]})]);}
            var Q1;
            Q1=makeQuery(id+"F5.boolean.opBoolean","SPLIT",FACE,{"disambiguationData":[TD([makeQuery(id+"F5.opExtrude","SWEPT_FACE",FACE,{"disambiguationData":[OSD([sQuery(id+"F4.wireOp",EDGE,"E41")])]})])],"derivedFrom":makeQuery(id+"F3.boolean.opBoolean","COPY",FACE,{"derivedFrom":makeQuery(id+"F3.opExtrude","CAP_FACE",FACE,{"disambiguationData":[OSD([sQuery(id+"F0.wireOp",EDGE,"E25.0"),sQuery(id+"F0.wireOp",EDGE,"E25.1"),sQuery(id+"F0.wireOp",EDGE,"E25.2"),sQuery(id+"F0.wireOp",EDGE,"E25.3"),sQuery(id+"F0.wireOp",EDGE,"E25.4"),sQuery(id+"F0.wireOp",EDGE,"E25.5"),sQuery(id+"F0.wireOp",EDGE,"E25.6"),sQuery(id+"F0.wireOp",EDGE,"E25.7")])],"isStart":false})})});
            extrude(context, id + "F13", {"entities" : qUnion([Q0]), "operationType" : NewBodyOperationType.REMOVE, "endBound" : BoundingType.UP_TO_SURFACE, "endBoundEntityFace" : qUnion([Q1]), "depth" : 25 * mm});
        }
        {
            var Q0;
            Q0=makeQuery(id+"F3.boolean.opBoolean","COPY",EDGE,{"derivedFrom":makeQuery(id+"F3.opExtrude","CAP_EDGE",EDGE,{"disambiguationData":[OSD([sQuery(id+"F0.wireOp",EDGE,"E25.6")])],"isStart":false})});
            var Q1;
            Q1=makeQuery(id+"F8.boolean.opBoolean","INTERSECT",EDGE,{"derivedFrom":[makeQuery(id+"F5.opExtrude","SWEPT_FACE",FACE,{"disambiguationData":[OSD([sQuery(id+"F4.wireOp",EDGE,"E30")])]}),makeQuery(id+"F8.opExtrude","CAP_FACE",FACE,{"disambiguationData":[OSD([sQuery(id+"F7.wireOp",EDGE,"E67")])],"isStart":false})]});
            var Q2;
            Q2=makeQuery(id+"F8.boolean.opBoolean","INTERSECT",EDGE,{"disambiguationData":[OD(1.0)],"derivedFrom":[makeQuery(id+"F5.opExtrude","SWEPT_FACE",FACE,{"disambiguationData":[OSD([sQuery(id+"F4.wireOp",EDGE,"E30")])]}),makeQuery(id+"F8.opExtrude","SWEPT_FACE",FACE,{"disambiguationData":[OSD([sQuery(id+"F7.wireOp",EDGE,"E67")])]})]});
            var Q3;
            {var subQ0=sQuery(id+"F4.wireOp",EDGE,"E30");Q3=makeQuery(id+"F8.boolean.opBoolean","SPLIT",EDGE,{"disambiguationData":[TD([makeQuery(id+"F5.opExtrude","SWEPT_FACE",FACE,{"disambiguationData":[OSD([sQuery(id+"F4.wireOp",EDGE,"E35.filletArc")])]})])],"derivedFrom":makeQuery(id+"F5.opExtrude","CAP_EDGE",EDGE,{"disambiguationData":[OSD([subQ0])],"isStart":false})});}
            var Q4;
            {var subQ0=sQuery(id+"F0.wireOp",EDGE,"E25.7");var subQ1=sQuery(id+"F0.wireOp",EDGE,"E25.1");var subQ2=sQuery(id+"F0.wireOp",EDGE,"E25.6");var subQ3=sQuery(id+"F0.wireOp",EDGE,"E25.5");var subQ4=sQuery(id+"F0.wireOp",EDGE,"E25.4");var subQ5=sQuery(id+"F0.wireOp",EDGE,"E25.0");var subQ6=sQuery(id+"F0.wireOp",EDGE,"E25.2");var subQ7=sQuery(id+"F0.wireOp",EDGE,"E25.3");Q4=makeQuery(id+"F8.boolean.opBoolean","INTERSECT",EDGE,{"derivedFrom":[makeQuery(id+"F5.boolean.opBoolean","SPLIT",FACE,{"disambiguationData":[TD([makeQuery(id+"F2.opExtrude","SWEPT_FACE",FACE,{"disambiguationData":[OSD([subQ5])]})])],"derivedFrom":makeQuery(id+"F3.boolean.opBoolean","COPY",FACE,{"derivedFrom":makeQuery(id+"F3.opExtrude","CAP_FACE",FACE,{"disambiguationData":[OSD([subQ5,subQ1,subQ6,subQ7,subQ4,subQ3,subQ2,subQ0])],"isStart":false})})}),makeQuery(id+"F8.opExtrude","SWEPT_FACE",FACE,{"disambiguationData":[OSD([sQuery(id+"F7.wireOp",EDGE,"E67")])]})]});}
            var Q5;
            Q5=makeQuery(id+"F8.boolean.opBoolean","INTERSECT",EDGE,{"disambiguationData":[OD(0.0)],"derivedFrom":[makeQuery(id+"F5.opExtrude","SWEPT_FACE",FACE,{"disambiguationData":[OSD([sQuery(id+"F4.wireOp",EDGE,"E30")])]}),makeQuery(id+"F8.opExtrude","SWEPT_FACE",FACE,{"disambiguationData":[OSD([sQuery(id+"F7.wireOp",EDGE,"E67")])]})]});
            fillet(context, id + "F14", {"entities" : qUnion([Q0, Q1, Q2, Q3, Q4, Q5]), "radius" : 3 * mm, "tangentPropagation" : true, "allowEdgeOverflow" : false});
        }
        {
            var Q0;
            Q0=makeQuery(id+"F1.opExtrude","CAP_EDGE",EDGE,{"disambiguationData":[OSD([sQuery(id+"F0.wireOp",EDGE,"E1.bottom")])],"isStart":false});
            fillet(context, id + "F15", {"entities" : qUnion([Q0]), "radius" : 2 * mm, "tangentPropagation" : true, "allowEdgeOverflow" : false});
        }
        {
            var Q0;
            Q0=qCreatedBy(makeId("Top.planeOp"),FACE);
            var sketch = newSketch(context, id + "F16", { "sketchPlane" : qUnion([Q0])});
            skCircle(sketch, "E79", {"center": v(0, 120) * mm, "radius": 6 * mm});
            skLineSegment(sketch, "E80.0", {"start": v(-70, 90) * mm, "end": v(70, 90) * mm});
            skArc(sketch, "E81.0", {"start": v(80, 80) * mm, "mid": v(77.07, 87.07) * mm, "end": v(70, 90) * mm});
            skLineSegment(sketch, "E81.1", {"start": v(80, -80) * mm, "end": v(80, 80) * mm});
            skArc(sketch, "E81.2", {"start": v(70, -90) * mm, "mid": v(77.07, -87.07) * mm, "end": v(80, -80) * mm});
            skLineSegment(sketch, "E81.3", {"start": v(-70, -90) * mm, "end": v(70, -90) * mm});
            skArc(sketch, "E81.4", {"start": v(-80, -80) * mm, "mid": v(-77.07, -87.07) * mm, "end": v(-70, -90) * mm});
            skLineSegment(sketch, "E81.5", {"start": v(-80, -80) * mm, "end": v(-80, 80) * mm});
            skArc(sketch, "E81.6", {"start": v(-70, 90) * mm, "mid": v(-77.07, 87.07) * mm, "end": v(-80, 80) * mm});
            skCircle(sketch, "E82.0", {"center": v(-60, 67.5) * mm, "radius": 4 * mm});
            skLineSegment(sketch, "E82.1", {"start": v(-60, 40.3) * mm, "end": v(-60, -40.3) * mm});
            skArc(sketch, "E82.2", {"start": v(-56.15, 48.18) * mm, "mid": v(-58.99, 44.68) * mm, "end": v(-60, 40.3) * mm});
            skArc(sketch, "E82.3", {"start": v(56.15, 48.18) * mm, "mid": v(0, 67.5) * mm, "end": v(-56.15, 48.18) * mm});
            skArc(sketch, "E82.4", {"start": v(60, 40.3) * mm, "mid": v(58.99, 44.68) * mm, "end": v(56.15, 48.18) * mm});
            skLineSegment(sketch, "E82.5", {"start": v(60, 40.3) * mm, "end": v(60, -40.3) * mm});
            skArc(sketch, "E82.6", {"start": v(56.15, -48.18) * mm, "mid": v(58.99, -44.68) * mm, "end": v(60, -40.3) * mm});
            skArc(sketch, "E82.7", {"start": v(-56.15, -48.18) * mm, "mid": v(0, -67.5) * mm, "end": v(56.15, -48.18) * mm});
            skArc(sketch, "E82.8", {"start": v(-60, -40.3) * mm, "mid": v(-58.99, -44.68) * mm, "end": v(-56.15, -48.18) * mm});
            skCircle(sketch, "E82.9", {"center": v(-60, -67.5) * mm, "radius": 4 * mm});
            skCircle(sketch, "E82.10", {"center": v(60, 67.5) * mm, "radius": 4 * mm});
            skCircle(sketch, "E82.11", {"center": v(60, -67.5) * mm, "radius": 4 * mm});
            skLineSegment(sketch, "E83", {"start": v(0, 120) * mm, "end": v(0, 90) * mm, "construction": true});
            skLineSegment(sketch, "E84", {"start": v(-33, 90) * mm, "end": v(-15, 108) * mm});
            skLineSegment(sketch, "E85", {"start": v(-15, 108) * mm, "end": v(-15, 120) * mm});
            skLineSegment(sketch, "E86", {"start": v(15, 120) * mm, "end": v(15, 108) * mm});
            skLineSegment(sketch, "E87", {"start": v(15, 108) * mm, "end": v(33, 90) * mm});
            skArc(sketch, "E88", {"start": v(15, 120) * mm, "mid": v(0, 135) * mm, "end": v(-15, 120) * mm});
            skLineSegment(sketch, "E89", {"start": v(-80, 0) * mm, "end": v(80, 0) * mm, "construction": true});
            skLineSegment(sketch, "E90.MirrorCS", {"start": v(15, -108) * mm, "end": v(33, -90) * mm});
            skLineSegment(sketch, "E91.MirrorCS", {"start": v(15, -120) * mm, "end": v(15, -108) * mm});
            skArc(sketch, "E92.MirrorCS", {"start": v(15, -120) * mm, "mid": v(0, -135) * mm, "end": v(-15, -120) * mm});
            skLineSegment(sketch, "E93.MirrorCS", {"start": v(-15, -108) * mm, "end": v(-15, -120) * mm});
            skLineSegment(sketch, "E94.MirrorCS", {"start": v(-33, -90) * mm, "end": v(-15, -108) * mm});
            skLineSegment(sketch, "E95.MirrorCS", {"start": v(0, -120) * mm, "end": v(0, -90) * mm, "construction": true});
            skCircle(sketch, "E96.MirrorC", {"center": v(0, -120) * mm, "radius": 6 * mm});
            skSolve(sketch);
        }
        {
            var Q0;
            Q0 = qSketchRegion(id + "F16", true);
            var Q1;
            Q1=makeQuery(id+"F2.opExtrude","CAP_FACE",FACE,{"disambiguationData":[OSD([sQuery(id+"F0.wireOp",EDGE,"E12"),sQuery(id+"F0.wireOp",EDGE,"E13"),sQuery(id+"F0.wireOp",EDGE,"E14"),sQuery(id+"F0.wireOp",EDGE,"E15"),sQuery(id+"F0.wireOp",EDGE,"E17.filletArc"),sQuery(id+"F0.wireOp",EDGE,"E18.filletArc"),sQuery(id+"F0.wireOp",EDGE,"E19.filletArc"),sQuery(id+"F0.wireOp",EDGE,"E20.filletArc"),sQuery(id+"F0.wireOp",EDGE,"E25.0"),sQuery(id+"F0.wireOp",EDGE,"E25.1"),sQuery(id+"F0.wireOp",EDGE,"E25.2"),sQuery(id+"F0.wireOp",EDGE,"E25.3"),sQuery(id+"F0.wireOp",EDGE,"E25.4"),sQuery(id+"F0.wireOp",EDGE,"E25.5"),sQuery(id+"F0.wireOp",EDGE,"E25.6"),sQuery(id+"F0.wireOp",EDGE,"E25.7")])],"isStart":false});
            extrude(context, id + "F17", {"entities" : qUnion([Q0]), "endBound" : BoundingType.UP_TO_SURFACE, "depth" : 25 * mm, "endBoundEntityFace" : qUnion([Q1]), "offsetDistance" : 25 * mm});
        }
    });
